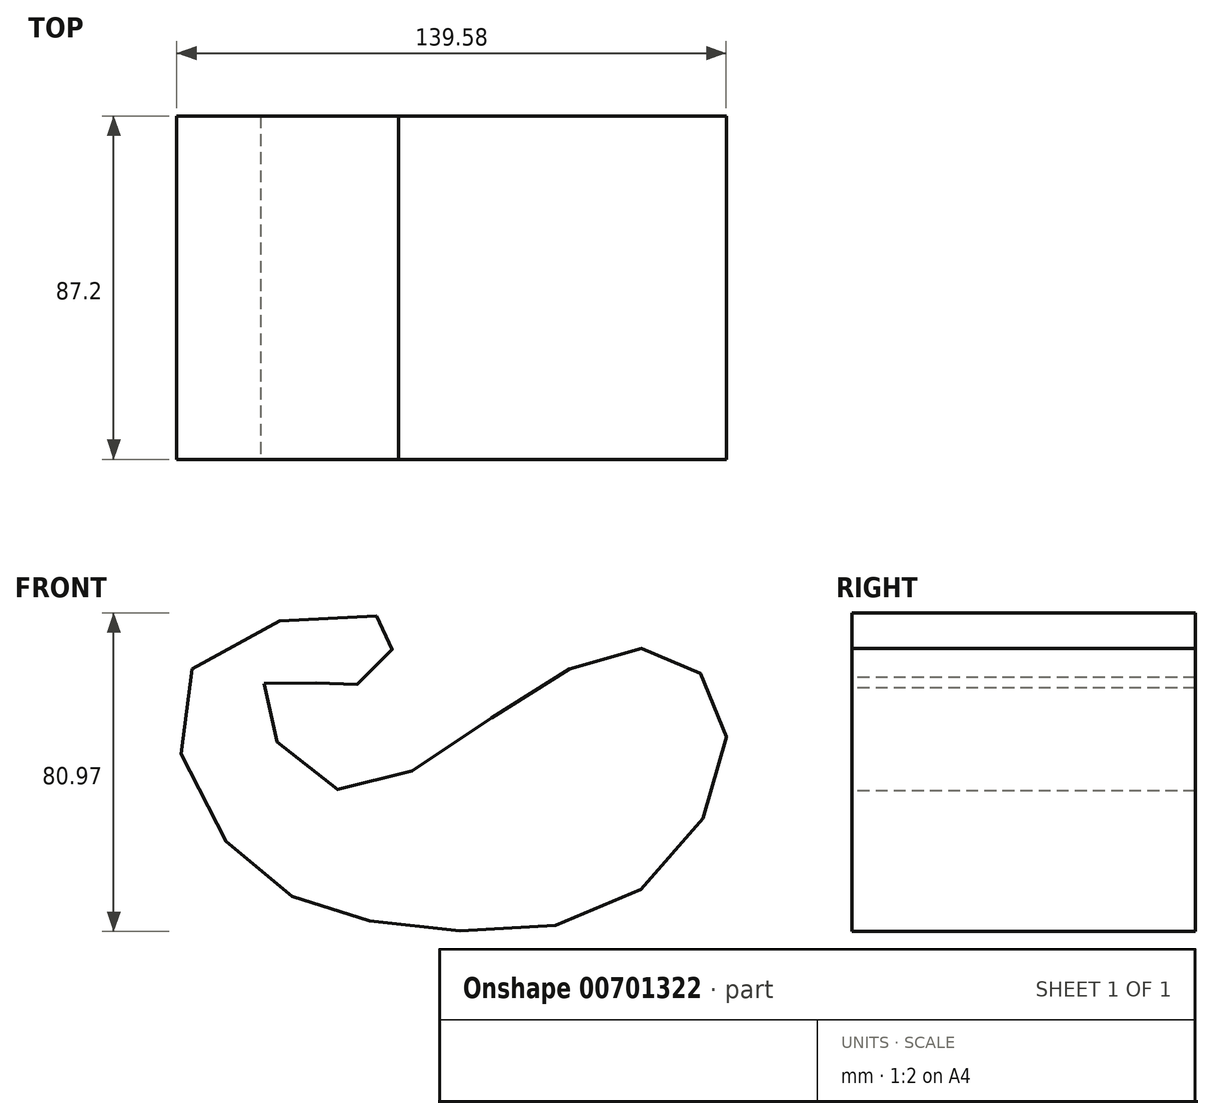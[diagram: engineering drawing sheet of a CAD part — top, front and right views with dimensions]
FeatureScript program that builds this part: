
annotation { "Feature Type Name" : "Feature", "Feature Type Description" : "" }
export const myFeature = defineFeature(function(context is Context, id is Id, definition is map)
    precondition{}
    {
        {
            var Q0;
            Q0=qCreatedBy(makeId("Front.planeOp"),FACE);
            var sketch = newSketch(context, id + "F0", { "sketchPlane" : qUnion([Q0])});
            skFitSpline(sketch, "E0", {"points": [v(-51.52, 38.15) * mm, v(-37.02, 12.53) * mm, v(5.28, 28.73) * mm, v(46.7, 46.97) * mm, v(65.64, 27.97) * mm, v(42.07, -15.67) * mm, v(-15.9, -23.44) * mm, v(-58.02, -5.63) * mm, v(-68.39, 43.61) * mm, v(-17.85, 52.68) * mm, v(-25.63, 39.72) * mm, v(-32.75, 37.13) * mm, v(-51.52, 38.15) * mm]});
            skSolve(sketch);
        }
        {
            var Q0;
            Q0 = qSketchRegion(id + "F0", true);
            extrude(context, id + "F1", {"entities" : qUnion([Q0]), "oppositeDirection" : true, "depth" : 87.2 * mm, "offsetDistance" : 25 * mm});
        }
    });
